# Revit family: PRD_FrankeWS_CntrTopWshBsns_RondoWashbasin_RNDH200-420,RNDX200-420
name_source: partatom
category: Plumbing Fixtures
revit_build: Autodesk Revit 2018 (Build: 20190510_1515(x64)
units: mm (PartAtom-declared; Revit-internal decimal feet)

## family parameters
Cut with Voids When Loaded = Yes
Host = Face
OmniClass Number = 23.45.05.14.14
OmniClass Title = Sinks/Lavatories
Part Type = Normal
Room Calculation Point = No
Round Connector Dimension = Use Diameter
Shared = No

## types (12) — shared parameters
AssetType = Fixed
Category = Pr_40_20_96_18, Counter top wash basins
Color = Stainless steel
DurationUnit = year
Form = Counter top wash basins
IfcExportAs = IfcSanitaryTerminalType
IfcExportType = WASHHANDBASIN
IntegralAccessories = Lugs for underneath mounting are included
Manufacturer = KWC Group AG
ManufacturerName = KWC Group AG
ManufacturerURL = www.kwc.com
Material = Stainless steel
MaterialsBody = Stainless steel 1.4301
NBSDescription = Counter top wash basins
NBSReference = 45-35-70/360
ProductInformation = https://pim.kwc.com
Shape = Round
URL = www.kwc.com
Uniclass2015Code = Pr_40_20_96_18
Uniclass2015Title = Counter top wash basins
Uniclass2015Version = Products v1.10
Version = 1
WarrantyDurationUnit = year
WashHandBasinMounting = CounterTop
WashHandBasinType = HandRinse
WasteSize = 32  [stored 0.104987 ft]
WaterSupplyOverflowAndWasteHolesOverflow = None
WaterSupplyOverflowAndWasteHolesWaste = Center-Center
WaterSupplyOverflowAndWasteHolesWaterSupply = No tapholes
zero-valued in all types: Default Elevation

## per-type parameters (varying)
| type | BIMObjectName | Description | DrainSize | Features | Finish | GrossWeight | MaterialsFinishAndColour | Model | ModelNumber | ModelReference | Name | NetWeight | NominalDepth | NominalHeight | NominalWidth | OutcutDiameterTop | OutcutDiameterUnderneath | OutcutHeight | Size | Type | WashbasinMaterial |
| RNDH200 - High polished | PRD_AR_CounterTopWashBasins_RondoWashbasin_RNDH200 | Round inset vanity basin, can be mounted from top or underneath, stainless steel, material thickness 1 mm, bowl diameter 200 mm, without overflow, incl. 5/4 flat perforated and plug waste, stainless steel lugs for underneath mounting are included. Outcut diameter for mounting from top: 212 mm, outcut diameter for mounting from underneath: 190 mm surface high-polished | DN 32 (1 1/4 inch.) | stainless steel, 1.00 mm, high polished, inset mounting, 233x108x233 mm (WxHxD) | High polished | 0.95 kg | High polished | RNDH200 | 2000056306 | RNDH200 | RONDO round inset vanity basin RNDH200 | 0.95 kg | 233 mm  [stored 0.764436 ft] | 108 mm  [stored 0.354331 ft] | 233 mm  [stored 0.764436 ft] | 212 mm  [stored 0.695538 ft] | 190 mm | 104 mm | 233x108x233 mm | RND200 | PRD_AR_StainlessSteel_HighPolished |
| RNDX200 - Satin finished | PRD_AR_CounterTopWashBasins_RondoWashbasin_RNDX200 | Round inset vanity basin, can be mounted from top or underneath, stainless steel, material thickness 1 mm, bowl diameter 200 mm, without overflow, incl. 5/4 flat perforated and plug waste, stainless steel lugs for underneath mounting are included. Outcut diameter for mounting from top: 212 mm, outcut diameter for mounting from underneath: 190 mm surface satin finished | DN-32-1-1-4INH | stainless steel, 1.00 mm, satin finished, inset mounting, 233x108x233 mm (WxHxD) | Satin finished | 0.95 kg | Satin finished | RNDX200 | 2000056331 | RNDX200 | RONDO round inset vanity basin RNDX200 | 0.95 kg | 233 mm  [stored 0.764436 ft] | 108 mm  [stored 0.354331 ft] | 233 mm  [stored 0.764436 ft] | 212 mm  [stored 0.695538 ft] | 190 mm | 104 mm | 233x108x233 mm | RND200 | PRD_AR_StainlessSteel_SatinFinished |
| RNDH260 - High polished | PRD_AR_CounterTopWashBasins_RondoWashbasin_RNDH260 | Round inset vanity basin, can be mounted from top or underneath, stainless steel, material thickness 1 mm, bowl diameter 260 mm, with overflow, incl. 5/4 overflow kit without waste, stainless steel lugs for underneath mounting are included. Outcut diameter for mounting from top: 274 mm, outcut diameter for mounting from underneath: 250 mm surface high-polished | DN-32-1-1-4INH | stainless steel, 1.00 mm, high polished, inset mounting, 295x118x295 mm (WxHxD) | High polished | 1.10 kg | High polished | RNDH260 | 2000056335 | RNDH260 | RONDO round inset vanity basin RNDH260 | 1.00 kg | 295 mm  [stored 0.967848 ft] | 118 mm | 295 mm  [stored 0.967848 ft] | 274 mm  [stored 0.89895 ft] | 250 mm  [stored 0.82021 ft] | 114 mm  [stored 0.374016 ft] | 295x118x295 mm | RND260 | PRD_AR_StainlessSteel_HighPolished |
| RNDX300 - Satin finished | PRD_AR_CounterTopWashBasins_RondoWashbasin_RNDX300 | Round inset vanity basin, can be mounted from top or underneath, stainless steel, material thickness 1 mm, bowl diameter 300 mm, with overflow, incl. 5/4 overflow kit without waste, stainless steel lugs for underneath mounting are included. Outcut diameter for mounting from top: 319 mm, outcut diameter for mounting from underneath: 290 mm surface satin finished | DN-32-1-1-4INH | stainless steel, 1.00 mm, satin finished, inset mounting, 339x160x339 mm (WxHxD) | Satin finished | 1.40 kg | Satin finished | RNDX300 | 2000056424 | RNDX300 | RONDO round inset vanity basin RNDX300 | 1.40 kg | 339 mm  [stored 1.1122 ft] | 160 mm  [stored 0.524934 ft] | 339 mm  [stored 1.1122 ft] | 319 mm  [stored 1.04659 ft] | 290 mm  [stored 0.951444 ft] | 155 mm  [stored 0.50853 ft] | 339x160x339 mm | RND300 | PRD_AR_StainlessSteel_SatinFinished |
| RNDX360 - Satin finished | PRD_AR_CounterTopWashBasins_RondoWashbasin_RNDX360 | Round inset vanity basin, can be mounted from top or underneath, stainless steel, material thickness 1 mm, bowl diameter 357 mm, with overflow, incl. 5/4 overflow kit without waste, stainless steel lugs for underneath mounting are included. Outcut diameter for mounting from top: 368 mm, outcut diameter for mounting from underneath: 350 mm surface satin finished | DN-32-1-1-4INH | stainless steel, 1.00 mm, satin finished, inset mounting, 388x150x388 mm (WxHxD) | Satin finished | 1.65 kg | Satin finished | RNDX360 | 2000056431 | RNDX360 | RONDO round inset vanity basin RNDX360 | 1.30 kg | 388 mm  [stored 1.27297 ft] | 150 mm | 388 mm  [stored 1.27297 ft] | 368 mm  [stored 1.20735 ft] | 350 mm  [stored 1.14829 ft] | 145 mm  [stored 0.475722 ft] | 388x150x388 mm | RND360 | PRD_AR_StainlessSteel_SatinFinished |
| RNDX420 - Satin finished | PRD_AR_CounterTopWashBasins_RondoWashbasin_RNDX420 | Round inset vanity basin, can be mounted from top or underneath, stainless steel, material thickness 1 mm, bowl diameter 418 mm, with overflow, incl. 5/4 overflow kit without waste, stainless steel lugs for underneath mounting are included. Outcut diameter for mounting from top: 436 mm, outcut diameter for mounting from underneath: 410 mm surface satin finished | DN-32-1-1-4INH | stainless steel, 1.00 mm, satin finished, inset mounting, 456x160x456 mm (WxHxD) | Satin finished | 2.70 kg | Satin finished | RNDX420 | 2000056537 | RNDX420 | RONDO round inset vanity basin RNDX420 | 2.50 kg | 456 mm  [stored 1.49606 ft] | 160 mm  [stored 0.524934 ft] | 456 mm  [stored 1.49606 ft] | 436 mm  [stored 1.43045 ft] | 410 mm  [stored 1.34514 ft] | 155 mm  [stored 0.50853 ft] | 456x160x456 mm | RND420 | PRD_AR_StainlessSteel_SatinFinished |
| RNDX381 - Satin finished | PRD_AR_CounterTopWashBasins_RondoWashbasin_RNDX381 | Round inset vanity basin, can be mounted from top or underneath, stainless steel, material thickness 1 mm, bowl diameter 380 mm, with overflow, incl. 5/4 overflow kit without waste, stainless steel lugs for underneath mounting are included. Outcut diameter for mounting from top: 408 mm, outcut diameter for mounting from underneath: 370 mm surface satin finished | DN-32-1-1-4INH | stainless steel, 1.00 mm, satin finished, inset mounting, 426x157x426 mm (WxHxD) | Satin finished | 2.14 kg | Satin finished | RNDX381 | 2000056436 | RNDX381 | RONDO round inset vanity basin RNDX381 | 1.90 kg | 426 mm  [stored 1.39764 ft] | 159 mm  [stored 0.521654 ft] | 426 mm  [stored 1.39764 ft] | 408 mm | 370 mm  [stored 1.21391 ft] | 154 mm  [stored 0.505249 ft] | 426x157x426 mm | RND381 | PRD_AR_StainlessSteel_SatinFinished |
| RNDX260 - Satin finished | PRD_AR_CounterTopWashBasins_RondoWashbasin_RNDX260 | Round inset vanity basin, can be mounted from top or underneath, stainless steel, material thickness 1 mm, bowl diameter 260 mm, with overflow, incl. 5/4 overflow kit without waste, stainless steel lugs for underneath mounting are included. Outcut diameter for mounting from top: 274 mm, outcut diameter for mounting from underneath: 250 mm surface satin finished | DN-32-1-1-4INH | stainless steel, 1.00 mm, satin finished, inset mounting, 295x118x295 mm (WxHxD) | Satin finished | 1.10 kg | Satin finished | RNDX260 | 2000056336 | RNDX260 | RONDO round inset vanity basin RNDX260 | 1.00 kg | 295 mm  [stored 0.967848 ft] | 118 mm | 295 mm  [stored 0.967848 ft] | 274 mm  [stored 0.89895 ft] | 250 mm  [stored 0.82021 ft] | 114 mm  [stored 0.374016 ft] | 295x118x295 mm | RND260 | PRD_AR_StainlessSteel_SatinFinished |
| RNDH300 - High polished | PRD_AR_CounterTopWashBasins_RondoWashbasin_RNDH300 | Round inset vanity basin, can be mounted from top or underneath, stainless steel, material thickness 1 mm, bowl diameter 300 mm, with overflow, incl. 5/4 overflow kit without waste, stainless steel lugs for underneath mounting are included. Outcut diameter for mounting from top: 319 mm, outcut diameter for mounting from underneath: 290 mm surface high-polished | DN-32-1-1-4INH | stainless steel, 1.00 mm, high polished, inset mounting, 339x160x339 mm (WxHxD) | High polished | 1.40 kg | High polished | RNDH300 | 2000056337 | RNDH300 | RONDO round inset vanity basin RNDH300 | 1.40 kg | 339 mm  [stored 1.1122 ft] | 160 mm  [stored 0.524934 ft] | 339 mm  [stored 1.1122 ft] | 319 mm  [stored 1.04659 ft] | 290 mm  [stored 0.951444 ft] | 155 mm  [stored 0.50853 ft] | 339x160x339 mm | RND300 | PRD_AR_StainlessSteel_HighPolished |
| RNDH360 - High polished | PRD_AR_CounterTopWashBasins_RondoWashbasin_RNDH360 | Round inset vanity basin, can be mounted from top or underneath, stainless steel, material thickness 1 mm, bowl diameter 357 mm, with overflow, incl. 5/4 overflow kit without waste, stainless steel lugs for underneath mounting are included. Outcut diameter for mounting from top: 368 mm, outcut diameter for mounting from underneath: 350 mm surface high-polished | DN-32-1-1-4INH | stainless steel, 1.00 mm, high polished, inset mounting, 388x150x388 mm (WxHxD) | High polished | 1.65 kg | High polished | RNDH360 | 2000056428 | RNDH360 | RONDO round inset vanity basin RNDH360 | 1.30 kg | 388 mm  [stored 1.27297 ft] | 150 mm | 388 mm  [stored 1.27297 ft] | 368 mm  [stored 1.20735 ft] | 350 mm  [stored 1.14829 ft] | 145 mm  [stored 0.475722 ft] | 388x150x388 mm | RND360 | PRD_AR_StainlessSteel_HighPolished |
| RNDH381 - High polished | PRD_AR_CounterTopWashBasins_RondoWashbasin_RNDH381 | Round inset vanity basin, can be mounted from top or underneath, stainless steel, material thickness 1 mm, bowl diameter 380 mm, with overflow, incl. 5/4 overflow kit without waste, stainless steel lugs for underneath mounting are included. Outcut diameter for mounting from top: 408 mm, outcut diameter for mounting from underneath: 370 mm surface high-polished | DN-32-1-1-4INH | stainless steel, 1.00 mm, high polished, inset mounting, 426x157x426 mm (WxHxD) | High polished | 2.20 kg | High polished | RNDH381 | 2000056432 | RNDH381 | RONDO round inset vanity basin RNDH381 | 2.20 kg | 426 mm  [stored 1.39764 ft] | 159 mm  [stored 0.521654 ft] | 426 mm  [stored 1.39764 ft] | 408 mm | 370 mm  [stored 1.21391 ft] | 154 mm  [stored 0.505249 ft] | 426x157x426 mm | RND381 | PRD_AR_StainlessSteel_HighPolished |
| RNDH420 - High polished | PRD_AR_CounterTopWashBasins_RondoWashbasin_RNDH420 | Round inset vanity basin, can be mounted from top or underneath, stainless steel, material thickness 1 mm, bowl diameter 418 mm, with overflow, incl. 5/4 overflow kit without waste, stainless steel lugs for underneath mounting are included. Outcut diameter for mounting from top: 436 mm, outcut diameter for mounting from underneath: 410 mm surface high-polished | DN-32-1-1-4INH | stainless steel, 1.00 mm, high polished, inset mounting, 456x160x456 mm (WxHxD) | High polished | 2.70 kg | High polished | RNDH420 | 2000056536 | RNDH420 | RONDO round inset vanity basin RNDH420 | 2.50 kg | 456 mm  [stored 1.49606 ft] | 160 mm  [stored 0.524934 ft] | 456 mm  [stored 1.49606 ft] | 436 mm  [stored 1.43045 ft] | 410 mm  [stored 1.34514 ft] | 155 mm  [stored 0.50853 ft] | 456x160x456 mm | RND420 | PRD_AR_StainlessSteel_HighPolished |

note: [stored X ft] marks values corroborated as IEEE doubles in the binary element streams (Revit-internal decimal feet)

## geometry (parser evidence)
native form markers: Sweep x21
no freeform markers — native parametric forms only
